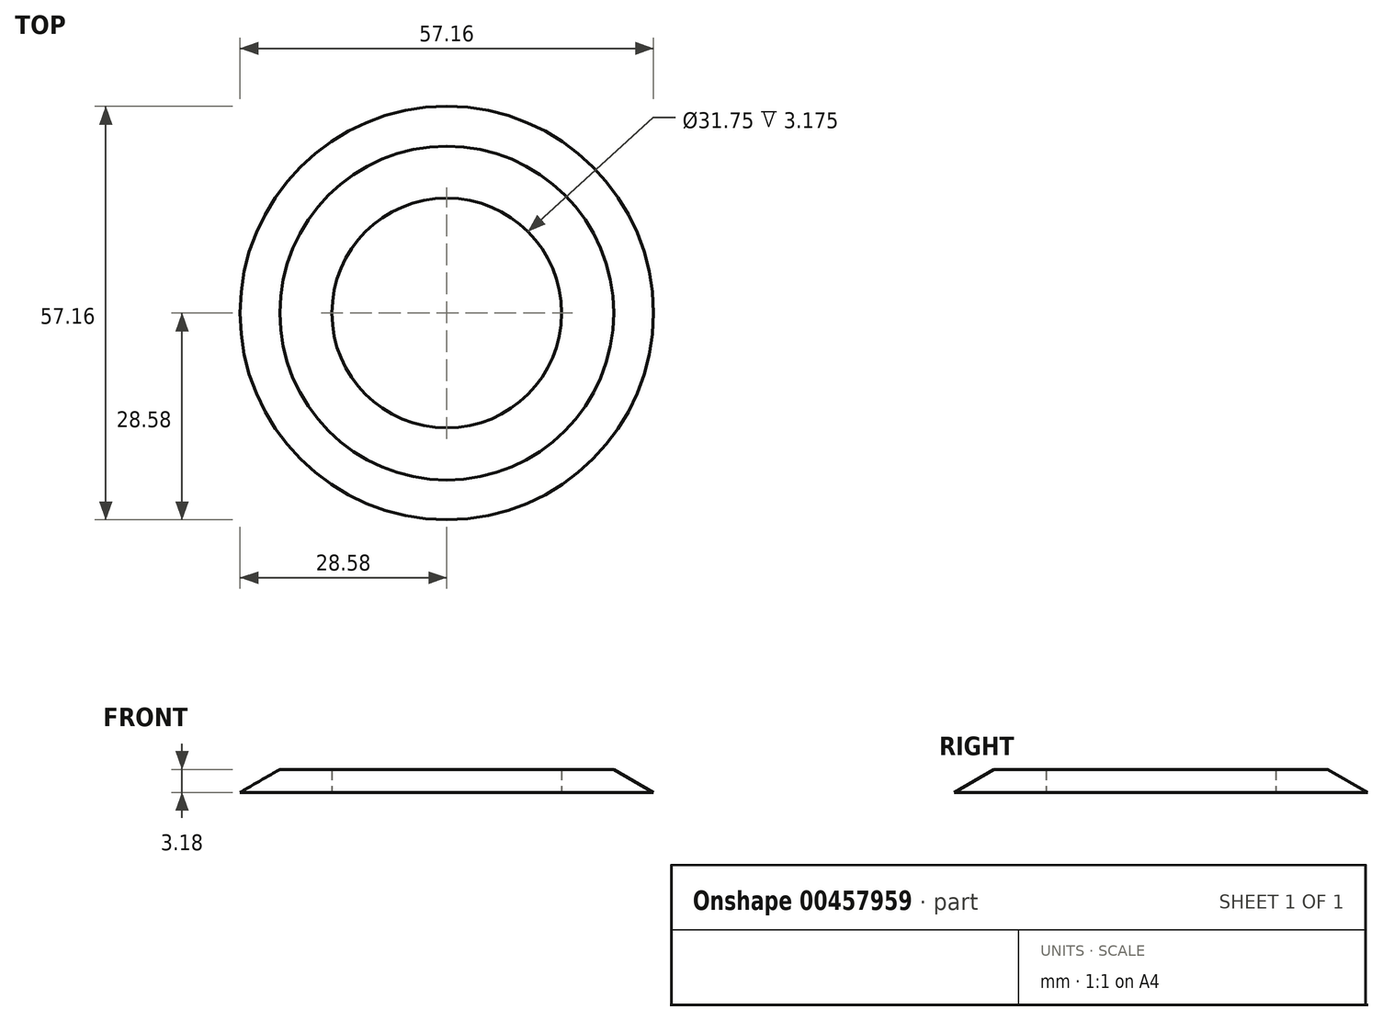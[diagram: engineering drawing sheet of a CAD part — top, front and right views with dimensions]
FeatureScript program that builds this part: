
annotation { "Feature Type Name" : "Feature", "Feature Type Description" : "" }
export const myFeature = defineFeature(function(context is Context, id is Id, definition is map)
    precondition{}
    {
        {
            var Q0;
            Q0=qCreatedBy(makeId("Front.planeOp"),FACE);
            var sketch = newSketch(context, id + "F0", { "sketchPlane" : qUnion([Q0])});
            skLineSegment(sketch, "E0", {"start": v(0, 0) * mm, "end": v(0, 29.1) * mm, "construction": true});
            skLineSegment(sketch, "E1", {"start": v(-15.88, 0) * mm, "end": v(-28.58, 0) * mm});
            skLineSegment(sketch, "E2", {"start": v(-28.58, 0) * mm, "end": v(-23.08, 3.18) * mm});
            skLineSegment(sketch, "E3", {"start": v(-23.08, 3.17) * mm, "end": v(-15.88, 3.17) * mm});
            skLineSegment(sketch, "E4", {"start": v(-15.88, 3.17) * mm, "end": v(-15.88, 0) * mm});
            skSolve(sketch);
        }
        {
            var Q0;
            Q0 = qSketchRegion(id + "F0", true);
            var Q1;
            Q1=sQuery(id+"F0.wireOp",EDGE,"E0");
            revolve(context, id + "F1", {"entities" : qUnion([Q0]), "axis" : qUnion([Q1]), "revolveType" : RevolveType.FULL});
        }
    });
